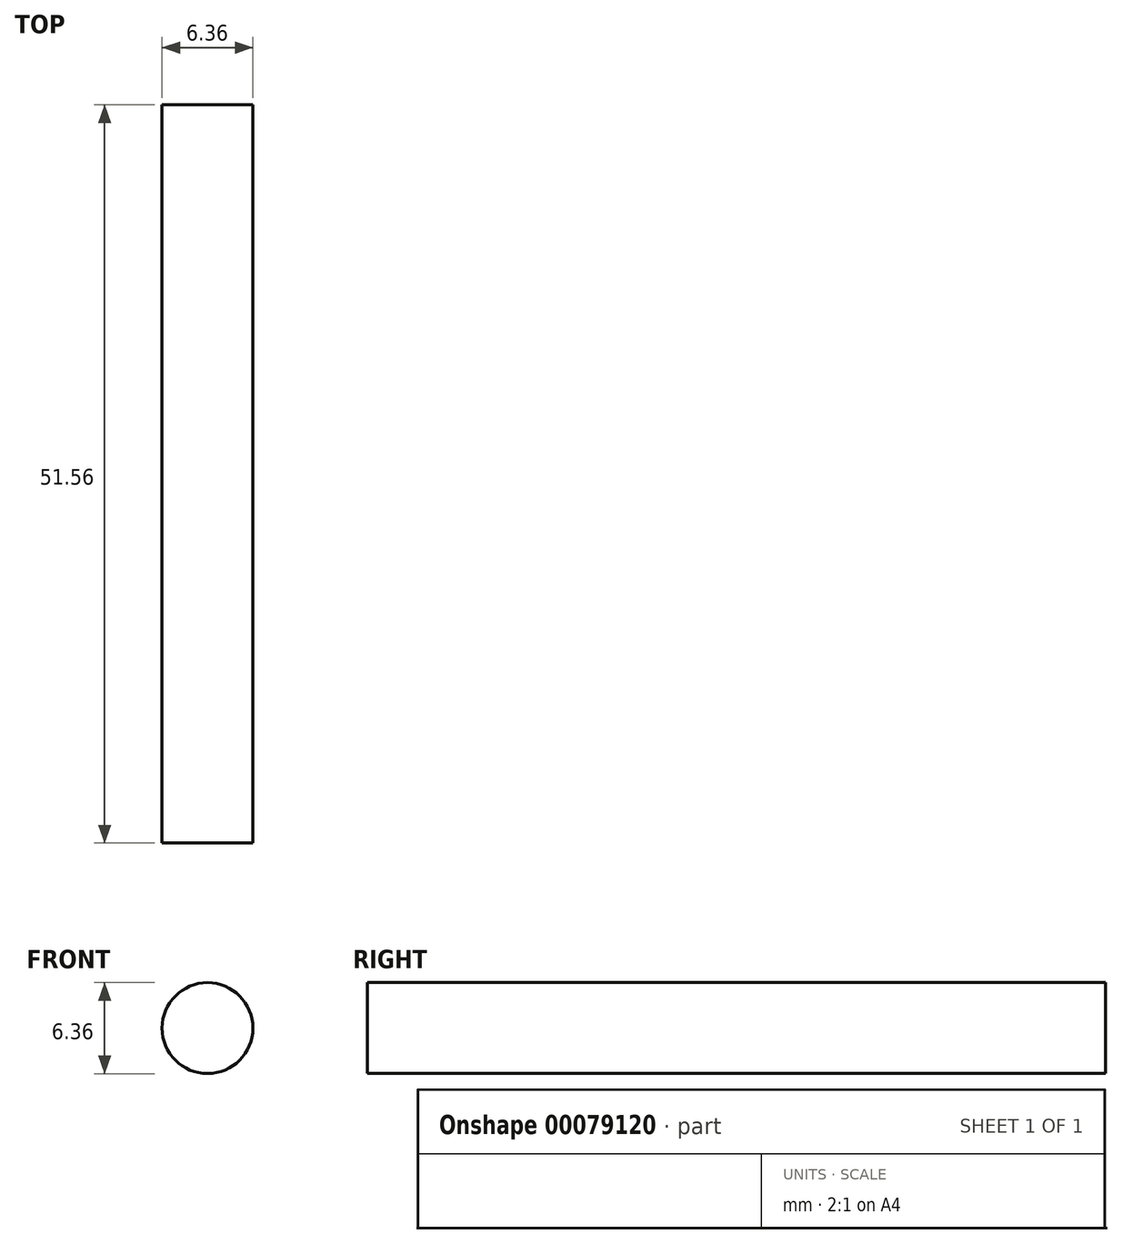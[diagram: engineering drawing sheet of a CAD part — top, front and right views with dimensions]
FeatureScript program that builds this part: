
annotation { "Feature Type Name" : "Feature", "Feature Type Description" : "" }
export const myFeature = defineFeature(function(context is Context, id is Id, definition is map)
    precondition{}
    {
        {
            var Q0;
            Q0=qCreatedBy(makeId("Front.planeOp"),FACE);
            var sketch = newSketch(context, id + "F0", { "sketchPlane" : qUnion([Q0])});
            skCircle(sketch, "E0", {"center": v(0, 0) * mm, "radius": 3.18 * mm});
            skSolve(sketch);
        }
        {
            var Q0;
            Q0 = qSketchRegion(id + "F0", true);
            extrude(context, id + "F1", {"entities" : qUnion([Q0]), "depth" : 51.56 * mm});
        }
    });
